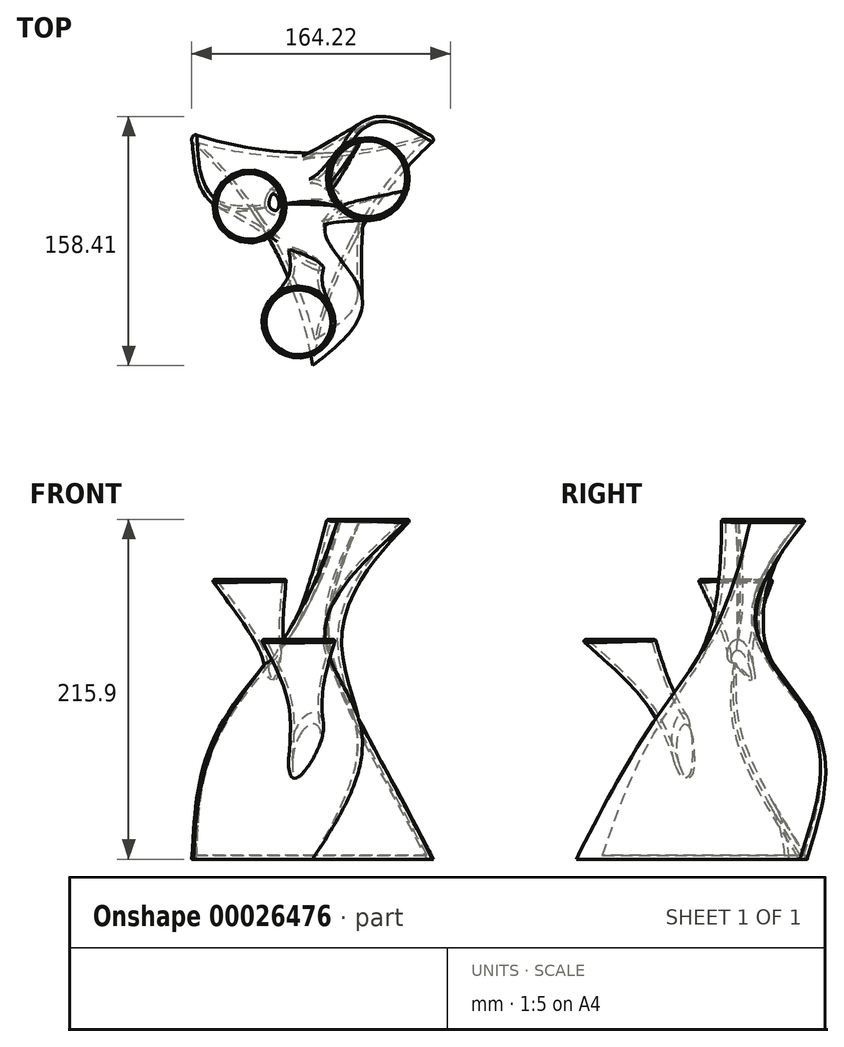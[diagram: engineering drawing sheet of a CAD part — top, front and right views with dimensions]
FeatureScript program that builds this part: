
annotation { "Feature Type Name" : "Feature", "Feature Type Description" : "" }
export const myFeature = defineFeature(function(context is Context, id is Id, definition is map)
    precondition{}
    {
        {
            var Q0;
            Q0=qCreatedBy(makeId("Top.planeOp"),FACE);
            var sketch = newSketch(context, id + "F0", { "sketchPlane" : qUnion([Q0])});
            skCircle(sketch, "E0.cCircle", {"center": v(0, 0) * mm, "radius": 50.55 * mm, "construction": true});
            skPoint(sketch, "E0.0.midPoint", {"position": v(43.8, -25.24) * mm});
            skArc(sketch, "E1", {"start": v(-87.59, 50.48) * mm, "mid": v(-0.03, 34.05) * mm, "end": v(87.5, 50.61) * mm});
            skArc(sketch, "E2.1.0", {"start": v(0.08, -101.1) * mm, "mid": v(-29.48, -17.05) * mm, "end": v(-87.59, 50.48) * mm});
            skArc(sketch, "E2.2.0", {"start": v(87.5, 50.61) * mm, "mid": v(29.5, -17) * mm, "end": v(0.08, -101.1) * mm});
            skSolve(sketch);
        }
        {
            var Q0;
            Q0=qCreatedBy(makeId("Top.planeOp"),FACE);
            cPlane(context, id + "F1", {"entities" : qUnion([Q0]), "cplaneType" : CPlaneType.OFFSET, "offset" : 177.8 * mm, "width" : 152.4 * mm, "height" : 152.4 * mm});
        }
        {
            var Q0;
            Q0=qCreatedBy(makeId("Top.planeOp"),FACE);
            cPlane(context, id + "F2", {"entities" : qUnion([Q0]), "cplaneType" : CPlaneType.OFFSET, "offset" : 88.9 * mm, "width" : 152.4 * mm, "height" : 152.4 * mm});
        }
        {
            var Q0;
            Q0=qCreatedBy(id+"F2.planeOp",FACE);
            var sketch = newSketch(context, id + "F3", { "sketchPlane" : qUnion([Q0])});
            skCircle(sketch, "E3.cCircle", {"center": v(0, 0) * mm, "radius": 29.33 * mm, "construction": true});
            skLineSegment(sketch, "E3.0", {"start": v(29.33, 50.8) * mm, "end": v(29.33, -50.8) * mm});
            skLineSegment(sketch, "E3.1", {"start": v(29.33, -50.8) * mm, "end": v(-58.66, 0) * mm});
            skLineSegment(sketch, "E3.2", {"start": v(-58.66, 0) * mm, "end": v(29.33, 50.8) * mm});
            skPoint(sketch, "E3.0.midPoint", {"position": v(29.33, 0) * mm});
            skSolve(sketch);
        }
        {
            var Q0;
            Q0=qCreatedBy(id+"F2.planeOp",FACE);
            cPlane(context, id + "F4", {"entities" : qUnion([Q0]), "cplaneType" : CPlaneType.OFFSET, "offset" : 50.8 * mm, "width" : 152.4 * mm, "height" : 152.4 * mm});
        }
        {
            var Q0;
            Q0=qCreatedBy(id+"F4.planeOp",FACE);
            var sketch = newSketch(context, id + "F5", { "sketchPlane" : qUnion([Q0])});
            skCircle(sketch, "E4", {"center": v(0, 0) * mm, "radius": 18.5 * mm});
            skSolve(sketch);
        }
        {
            var Q0;
            Q0=qCreatedBy(id+"F2.planeOp",FACE);
            var sketch = newSketch(context, id + "F6", { "sketchPlane" : qUnion([Q0])});
            skCircle(sketch, "E5", {"center": v(-11.28, 5.02) * mm, "radius": 19.31 * mm});
            skSolve(sketch);
        }
        {
            var Q0;
            Q0=qCreatedBy(id+"F1.planeOp",FACE);
            var sketch = newSketch(context, id + "F7", { "sketchPlane" : qUnion([Q0])});
            skCircle(sketch, "E6", {"center": v(-40.54, 0) * mm, "radius": 23.9 * mm});
            skSolve(sketch);
        }
        {
            var Q0;
            Q0=qCreatedBy(id+"F4.planeOp",FACE);
            var sketch = newSketch(context, id + "F8", { "sketchPlane" : qUnion([Q0])});
            skCircle(sketch, "E7", {"center": v(-9.09, -74.57) * mm, "radius": 23.73 * mm});
            skSolve(sketch);
        }
        {
            var Q0;
            Q0=qCreatedBy(id+"F2.planeOp",FACE);
            var sketch = newSketch(context, id + "F9", { "sketchPlane" : qUnion([Q0])});
            skCircle(sketch, "E8", {"center": v(-3.8, -39.96) * mm, "radius": 10.37 * mm});
            skSolve(sketch);
        }
        {
            var Q0;
            Q0=qCreatedBy(makeId("Top.planeOp"),FACE);
            var sketch = newSketch(context, id + "F10", { "sketchPlane" : qUnion([Q0])});
            skCircle(sketch, "E9", {"center": v(0, 0) * mm, "radius": 21.37 * mm});
            skSolve(sketch);
        }
        {
            var Q0;
            Q0=qCreatedBy(id+"F1.planeOp",FACE);
            cPlane(context, id + "F11", {"entities" : qUnion([Q0]), "cplaneType" : CPlaneType.OFFSET, "offset" : 38.1 * mm, "width" : 152.4 * mm, "height" : 152.4 * mm});
        }
        {
            var Q0;
            Q0=qCreatedBy(id+"F11.planeOp",FACE);
            var sketch = newSketch(context, id + "F12", { "sketchPlane" : qUnion([Q0])});
            skCircle(sketch, "E10", {"center": v(36.22, 18.12) * mm, "radius": 26.97 * mm});
            skSolve(sketch);
        }
        {
            var Q0;
            Q0=makeQuery(id+"F12.imprint","IMPRINT",FACE,{"disambiguationData":[TD([[makeQuery(id+"F12.imprint","IMPRINT",EDGE,{"derivedFrom":sQuery(id+"F12.wireOp",EDGE,"E10")}),1.0]])]});
            var Q1;
            Q1=makeQuery(id+"F5.imprint","IMPRINT",FACE,{"disambiguationData":[TD([[makeQuery(id+"F5.imprint","IMPRINT",EDGE,{"derivedFrom":sQuery(id+"F5.wireOp",EDGE,"E4")}),1.0]])]});
            var Q2;
            Q2=makeQuery(id+"F3.imprint","IMPRINT",FACE,{"disambiguationData":[TD([[makeQuery(id+"F3.imprint","IMPRINT",EDGE,{"derivedFrom":sQuery(id+"F3.wireOp",EDGE,"E3.0")}),-1.0]])]});
            var Q3;
            Q3=makeQuery(id+"F0.imprint","IMPRINT",FACE,{"disambiguationData":[TD([[makeQuery(id+"F0.imprint","IMPRINT",EDGE,{"derivedFrom":sQuery(id+"F0.wireOp",EDGE,"E1")}),-1.0]])]});
            loft(context, id + "F13", {"sheetProfilesArray" : [{ "sheetProfileEntities" : qUnion([Q0]) }, { "sheetProfileEntities" : qUnion([Q1]) }, { "sheetProfileEntities" : qUnion([Q2]) }, { "sheetProfileEntities" : qUnion([Q3]) }]});
        }
        {
            var Q1;
            Q1=makeQuery(id+"F8.imprint","IMPRINT",FACE,{"disambiguationData":[TD([[makeQuery(id+"F8.imprint","IMPRINT",EDGE,{"derivedFrom":sQuery(id+"F8.wireOp",EDGE,"E7")}),1.0]])]});
            var Q2;
            Q2=makeQuery(id+"F9.imprint","IMPRINT",FACE,{"disambiguationData":[TD([[makeQuery(id+"F9.imprint","IMPRINT",EDGE,{"derivedFrom":sQuery(id+"F9.wireOp",EDGE,"E8")}),1.0]])]});
            var Q3;
            Q3=makeQuery(id+"F10.imprint","IMPRINT",FACE,{"disambiguationData":[TD([[makeQuery(id+"F10.imprint","IMPRINT",EDGE,{"derivedFrom":sQuery(id+"F10.wireOp",EDGE,"E9")}),1.0]])]});
            loft(context, id + "F14", {"operationType" : NewBodyOperationType.ADD, "sheetProfilesArray" : [{ "sheetProfileEntities" : qUnion([Q1]) }, { "sheetProfileEntities" : qUnion([Q2]) }, { "sheetProfileEntities" : qUnion([Q3]) }]});
        }
        {
            var Q1;
            Q1=makeQuery(id+"F7.imprint","IMPRINT",FACE,{"disambiguationData":[TD([[makeQuery(id+"F7.imprint","IMPRINT",EDGE,{"derivedFrom":sQuery(id+"F7.wireOp",EDGE,"E6")}),1.0]])]});
            var Q2;
            Q2 = qSketchRegion(id + "F6", true);
            loft(context, id + "F15", {"operationType" : NewBodyOperationType.ADD, "sheetProfilesArray" : [{ "sheetProfileEntities" : qUnion([Q1]) }, { "sheetProfileEntities" : qUnion([Q2]) }]});
        }
        {
            var Q0;
            {var subQ0=sQuery(id+"F3.wireOp",EDGE,"E3.0");var subQ1=sQuery(id+"F3.wireOp",EDGE,"E3.1");var subQ2=sQuery(id+"F3.wireOp",EDGE,"E3.2");var subQ3=sQuery(id+"F5.wireOp",EDGE,"E4");Q0=makeQuery(id+"F13.opLoft","SWEPT_EDGE",EDGE,{"disambiguationData":[OSD([subQ0,subQ1,subQ2,subQ3]),TDD([makeQuery(id+"F3.imprint","INTERSECT",VERTEX,{"derivedFrom":[subQ0,subQ2]}),makeQuery(id+"F3.imprint","INTERSECT",VERTEX,{"derivedFrom":[subQ0,subQ1]}),makeQuery(id+"F5.imprint","IMPRINT",EDGE,{"derivedFrom":subQ3})])]});}
            var Q1;
            Q1=makeQuery(id+"F13.opLoft","SWEPT_EDGE",EDGE,{"disambiguationData":[OSD([sQuery(id+"F3.wireOp",EDGE,"E3.0"),sQuery(id+"F3.wireOp",EDGE,"E3.2")]),OD(0.0)]});
            var Q2;
            {var subQ0=sQuery(id+"F3.wireOp",EDGE,"E3.0");var subQ1=sQuery(id+"F3.wireOp",EDGE,"E3.1");var subQ2=sQuery(id+"F3.wireOp",EDGE,"E3.2");var subQ3=sQuery(id+"F5.wireOp",EDGE,"E4");Q2=makeQuery(id+"F15.boolean.opBoolean","SPLIT",EDGE,{"disambiguationData":[OD(1.0)],"derivedFrom":makeQuery(id+"F13.opLoft","SWEPT_EDGE",EDGE,{"disambiguationData":[OSD([subQ0,subQ1,subQ2,subQ3]),TDD([makeQuery(id+"F3.imprint","INTERSECT",VERTEX,{"derivedFrom":[subQ0,subQ1]}),makeQuery(id+"F3.imprint","INTERSECT",VERTEX,{"derivedFrom":[subQ1,subQ2]}),makeQuery(id+"F5.imprint","IMPRINT",EDGE,{"derivedFrom":subQ3})])]})});}
            fillet(context, id + "F16", {"entities" : qUnion([Q0, Q1, Q2]), "radius" : 2.54 * mm, "allowEdgeOverflow" : false});
        }
        {
            var Q0;
            Q0=makeQuery(id+"F13.opLoft","CAP_FACE",FACE,{"disambiguationData":[OSD([makeQuery(id+"F12.imprint","IMPRINT",FACE,{"disambiguationData":[TD([[makeQuery(id+"F12.imprint","IMPRINT",EDGE,{"derivedFrom":sQuery(id+"F12.wireOp",EDGE,"E10")}),1.0]])]})])],"isStart":true});
            var Q1;
            Q1=makeQuery(id+"F15.opLoft","CAP_FACE",FACE,{"disambiguationData":[OSD([makeQuery(id+"F7.imprint","IMPRINT",FACE,{"disambiguationData":[TD([[makeQuery(id+"F7.imprint","IMPRINT",EDGE,{"derivedFrom":sQuery(id+"F7.wireOp",EDGE,"E6")}),1.0]])]})])],"isStart":true});
            var Q2;
            Q2=makeQuery(id+"F14.opLoft","CAP_FACE",FACE,{"disambiguationData":[OSD([makeQuery(id+"F8.imprint","IMPRINT",FACE,{"disambiguationData":[TD([[makeQuery(id+"F8.imprint","IMPRINT",EDGE,{"derivedFrom":sQuery(id+"F8.wireOp",EDGE,"E7")}),1.0]])]})])],"isStart":true});
            shell(context, id + "F17", {"entities" : qUnion([Q0, Q1, Q2]), "thickness" : 2.54 * mm});
        }
        {
            var Q0;
            Q0=makeQuery(id+"F13.opLoft","CAP_FACE",FACE,{"disambiguationData":[OSD([makeQuery(id+"F12.imprint","IMPRINT",FACE,{"disambiguationData":[TD([[makeQuery(id+"F12.imprint","IMPRINT",EDGE,{"derivedFrom":sQuery(id+"F12.wireOp",EDGE,"E10")}),1.0]])]})])],"isStart":true});
            var Q1;
            Q1=makeQuery(id+"F15.opLoft","CAP_FACE",FACE,{"disambiguationData":[OSD([makeQuery(id+"F7.imprint","IMPRINT",FACE,{"disambiguationData":[TD([[makeQuery(id+"F7.imprint","IMPRINT",EDGE,{"derivedFrom":sQuery(id+"F7.wireOp",EDGE,"E6")}),1.0]])]})])],"isStart":true});
            var Q2;
            Q2=makeQuery(id+"F14.opLoft","CAP_FACE",FACE,{"disambiguationData":[OSD([makeQuery(id+"F8.imprint","IMPRINT",FACE,{"disambiguationData":[TD([[makeQuery(id+"F8.imprint","IMPRINT",EDGE,{"derivedFrom":sQuery(id+"F8.wireOp",EDGE,"E7")}),1.0]])]})])],"isStart":true});
            fillet(context, id + "F18", {"entities" : qUnion([Q0, Q1, Q2]), "radius" : 1.27 * mm, "tangentPropagation" : true, "allowEdgeOverflow" : false});
        }
    });
